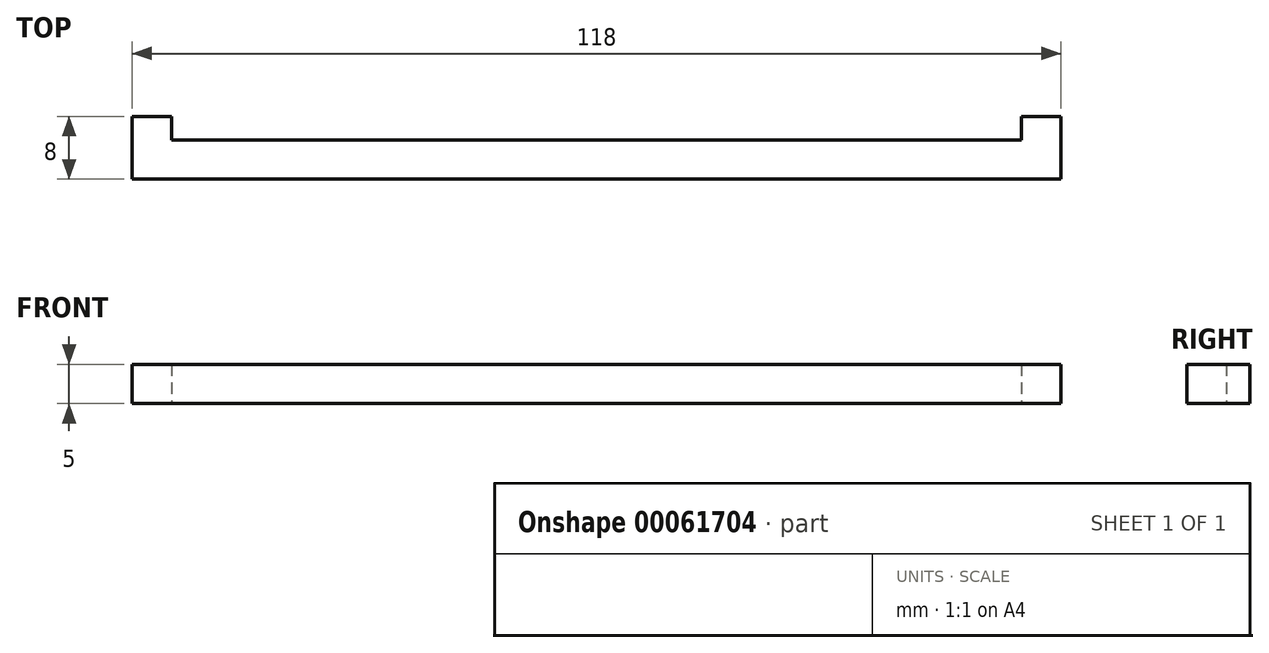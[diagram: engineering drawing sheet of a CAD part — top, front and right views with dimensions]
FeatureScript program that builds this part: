
annotation { "Feature Type Name" : "Feature", "Feature Type Description" : "" }
export const myFeature = defineFeature(function(context is Context, id is Id, definition is map)
    precondition{}
    {
        {
            var Q0;
            Q0=qCreatedBy(makeId("Top.planeOp"),FACE);
            var sketch = newSketch(context, id + "F0", { "sketchPlane" : qUnion([Q0])});
            skLineSegment(sketch, "E0", {"start": v(0, 0) * mm, "end": v(118, 0) * mm});
            skLineSegment(sketch, "E1", {"start": v(118, 0) * mm, "end": v(118, 8) * mm});
            skLineSegment(sketch, "E2", {"start": v(118, 8) * mm, "end": v(113, 8) * mm});
            skLineSegment(sketch, "E3", {"start": v(113, 8) * mm, "end": v(113, 5) * mm});
            skLineSegment(sketch, "E4", {"start": v(113, 5) * mm, "end": v(5, 5) * mm});
            skLineSegment(sketch, "E5", {"start": v(5, 5) * mm, "end": v(5, 8) * mm});
            skLineSegment(sketch, "E6", {"start": v(5, 8) * mm, "end": v(0, 8) * mm});
            skLineSegment(sketch, "E7", {"start": v(0, 8) * mm, "end": v(0, 0) * mm});
            skSolve(sketch);
        }
        {
            var Q0;
            Q0 = qSketchRegion(id + "F0", true);
            extrude(context, id + "F1", {"entities" : qUnion([Q0]), "depth" : 5 * mm});
        }
    });
